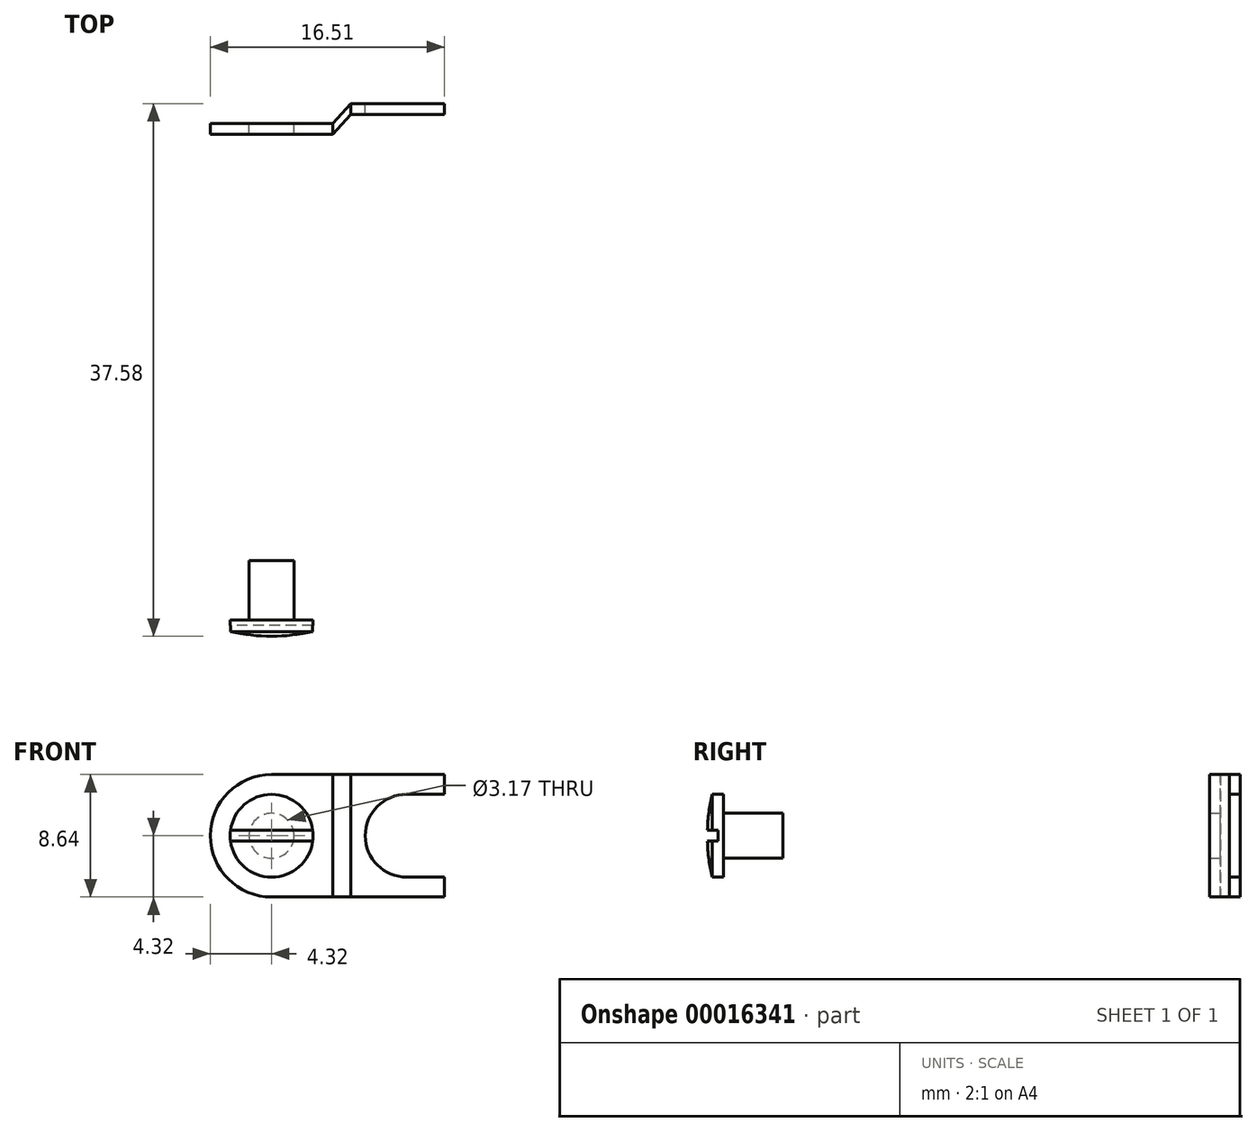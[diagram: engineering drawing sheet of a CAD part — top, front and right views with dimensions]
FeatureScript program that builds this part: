
annotation { "Feature Type Name" : "Feature", "Feature Type Description" : "" }
export const myFeature = defineFeature(function(context is Context, id is Id, definition is map)
    precondition{}
    {
        {
            var Q0;
            Q0=qCreatedBy(makeId("Front.planeOp"),FACE);
            var sketch = newSketch(context, id + "F0", { "sketchPlane" : qUnion([Q0])});
            skLineSegment(sketch, "E0.rect.bottom", {"start": v(4.32, -4.32) * mm, "end": v(0, -4.32) * mm});
            skLineSegment(sketch, "E0.rect.top", {"start": v(4.32, 4.32) * mm, "end": v(0, 4.32) * mm});
            skLineSegment(sketch, "E0.rect.left", {"start": v(4.32, -4.32) * mm, "end": v(4.32, 4.32) * mm});
            skLineSegment(sketch, "E0.rect.right", {"start": v(-4.32, 0) * mm, "end": v(-4.32, 0) * mm});
            skPoint(sketch, "E0.rect.middle", {"position": v(0, 0) * mm});
            skLineSegment(sketch, "E1.bottom", {"start": v(4.32, 4.32) * mm, "end": v(5.59, 4.32) * mm, "construction": true});
            skLineSegment(sketch, "E1.top", {"start": v(4.32, -4.32) * mm, "end": v(5.59, -4.32) * mm, "construction": true});
            skLineSegment(sketch, "E1.left", {"start": v(4.32, 4.32) * mm, "end": v(4.32, -4.32) * mm, "construction": true});
            skLineSegment(sketch, "E1.right", {"start": v(5.59, 4.32) * mm, "end": v(5.59, -4.32) * mm, "construction": true});
            skLineSegment(sketch, "E2.bottom", {"start": v(5.59, 4.32) * mm, "end": v(12.2, 4.32) * mm, "construction": true});
            skLineSegment(sketch, "E2.top", {"start": v(5.59, -4.32) * mm, "end": v(12.2, -4.32) * mm, "construction": true});
            skLineSegment(sketch, "E2.right", {"start": v(12.2, 4.32) * mm, "end": v(12.2, -4.32) * mm, "construction": true});
            skCircle(sketch, "E3", {"center": v(0, 0) * mm, "radius": 1.59 * mm});
            skPoint(sketch, "E4.visualSharp", {"position": v(-4.32, 4.32) * mm});
            skArc(sketch, "E4.filletArc", {"start": v(0, 4.32) * mm, "mid": v(-3.05, 3.05) * mm, "end": v(-4.32, 0) * mm});
            skPoint(sketch, "E5.visualSharp", {"position": v(-4.32, -4.32) * mm});
            skArc(sketch, "E5.filletArc", {"start": v(-4.32, 0) * mm, "mid": v(-3.05, -3.05) * mm, "end": v(0, -4.32) * mm});
            skSolve(sketch);
        }
        {
            var Q0;
            Q0=makeQuery(id+"F0.imprint","IMPRINT",FACE,{"disambiguationData":[TD([[makeQuery(id+"F0.imprint","IMPRINT",EDGE,{"derivedFrom":sQuery(id+"F0.wireOp",EDGE,"E0.rect.bottom")}),-1.0]])]});
            cPlane(context, id + "F1", {"entities" : qUnion([Q0]), "cplaneType" : CPlaneType.OFFSET, "offset" : 1.4 * mm, "oppositeDirection" : true, "width" : 152.4 * mm, "height" : 152.4 * mm});
        }
        {
            var Q0;
            Q0=qCreatedBy(id+"F1.planeOp",FACE);
            var sketch = newSketch(context, id + "F2", { "sketchPlane" : qUnion([Q0])});
            skPoint(sketch, "E6.0", {"position": v(5.59, 4.32) * mm});
            skPoint(sketch, "E7.0", {"position": v(5.59, -4.32) * mm});
            skPoint(sketch, "E8.0", {"position": v(12.2, -4.32) * mm});
            skPoint(sketch, "E9.0", {"position": v(12.2, 4.32) * mm});
            skLineSegment(sketch, "E10.bottom", {"start": v(5.59, 4.32) * mm, "end": v(12.2, 4.32) * mm});
            skLineSegment(sketch, "E10.top", {"start": v(5.59, -4.32) * mm, "end": v(12.2, -4.32) * mm});
            skLineSegment(sketch, "E10.left", {"start": v(5.59, 4.32) * mm, "end": v(5.59, -4.32) * mm});
            skLineSegment(sketch, "E10.right", {"start": v(12.2, 4.32) * mm, "end": v(12.2, -4.32) * mm});
            skLineSegment(sketch, "E11", {"start": v(12.2, 2.92) * mm, "end": v(5.59, 2.92) * mm});
            skPoint(sketch, "E12.0", {"position": v(0, 0) * mm});
            skLineSegment(sketch, "E13", {"start": v(5.59, 0) * mm, "end": v(12.2, 0) * mm, "construction": true});
            skLineSegment(sketch, "E14.MirrorCS", {"start": v(12.2, -2.92) * mm, "end": v(5.59, -2.92) * mm});
            skCircle(sketch, "E15", {"center": v(9.53, 0) * mm, "radius": 2.92 * mm});
            skSolve(sketch);
        }
        {
            var Q0;
            Q0 = qSketchRegion(id + "F0", true);
            extrude(context, id + "F3", {"entities" : qUnion([Q0]), "depth" : 0.76 * mm});
        }
        {
            var Q0;
            {var subQ6=sQuery(id+"F2.wireOp",EDGE,"E10.bottom");Q0=makeQuery(id+"F2.imprint","IMPRINT",FACE,{"disambiguationData":[TD([[makeQuery(id+"F2.imprint","IMPRINT",EDGE,{"derivedFrom":subQ6}),-1.0]])]});}
            var Q1;
            {var subQ6=sQuery(id+"F2.wireOp",EDGE,"E10.top");Q1=makeQuery(id+"F2.imprint","IMPRINT",FACE,{"disambiguationData":[TD([[makeQuery(id+"F2.imprint","IMPRINT",EDGE,{"derivedFrom":subQ6}),1.0]])]});}
            var Q2;
            {var subQ3=sQuery(id+"F2.wireOp",EDGE,"E11");var subQ5=sQuery(id+"F2.wireOp",EDGE,"E10.left");var subQ7=makeQuery(id+"F2.imprint","INTERSECT",VERTEX,{"derivedFrom":[subQ5,subQ3]});Q2=makeQuery(id+"F2.imprint","IMPRINT",FACE,{"disambiguationData":[TD([[makeQuery(id+"F2.imprint","IMPRINT",EDGE,{"disambiguationData":[TD([[subQ7,-1.0]])],"derivedFrom":subQ5}),1.0]])]});}
            extrude(context, id + "F4", {"entities" : qUnion([Q0, Q1, Q2]), "depth" : 0.76 * mm});
        }
        {
            var Q0;
            Q0=makeQuery(id+"F3.opExtrude","SWEPT_FACE",FACE,{"disambiguationData":[OSD([sQuery(id+"F0.wireOp",EDGE,"E0.rect.left")])]});
            var Q1;
            Q1=makeQuery(id+"F4.opExtrude","SWEPT_FACE",FACE,{"disambiguationData":[OSD([sQuery(id+"F2.wireOp",EDGE,"E10.left")])]});
            loft(context, id + "F5", {"sheetProfilesArray" : [{ "sheetProfileEntities" : qUnion([Q0]) }, { "sheetProfileEntities" : qUnion([Q1]) }]});
        }
        {
            var Q0;
            Q0=qCreatedBy(makeId("Right.planeOp"),FACE);
            var sketch = newSketch(context, id + "F6", { "sketchPlane" : qUnion([Q0])});
            skLineSegment(sketch, "E16.bottom", {"start": v(-35.04, 1.59) * mm, "end": v(-30.85, 1.59) * mm});
            skLineSegment(sketch, "E16.top", {"start": v(-35.04, 0) * mm, "end": v(-30.85, 0) * mm});
            skLineSegment(sketch, "E16.left", {"start": v(-35.04, 1.59) * mm, "end": v(-35.04, 0) * mm});
            skLineSegment(sketch, "E16.right", {"start": v(-30.85, 1.59) * mm, "end": v(-30.85, 0) * mm});
            skLineSegment(sketch, "E17.bottom", {"start": v(-36.18, 2.92) * mm, "end": v(-35.04, 2.92) * mm});
            skLineSegment(sketch, "E17.top", {"start": v(-36.18, 0) * mm, "end": v(-35.04, 0) * mm});
            skLineSegment(sketch, "E17.left", {"start": v(-36.18, 2.92) * mm, "end": v(-36.18, 0) * mm});
            skLineSegment(sketch, "E17.right", {"start": v(-35.04, 2.92) * mm, "end": v(-35.04, 0) * mm});
            skCircle(sketch, "E18", {"center": v(-23.48, 0) * mm, "radius": 12.7 * mm});
            skLineSegment(sketch, "E19", {"start": v(-36.18, 0) * mm, "end": v(-36.18, 2.92) * mm, "construction": true});
            skSolve(sketch);
        }
        {
            var Q0;
            Q0=qCreatedBy(makeId("Front.planeOp"),FACE);
            var Q1;
            Q1=sQuery(id+"F6.wireOp",VERTEX,"E17.top.start");
            cPlane(context, id + "F7", {"entities" : qUnion([Q0, Q1]), "cplaneType" : CPlaneType.PLANE_POINT, "offset" : 152.4 * mm, "width" : 152.4 * mm, "height" : 152.4 * mm});
        }
        {
            var Q0;
            {var subQ1=sQuery(id+"F6.wireOp",EDGE,"E17.top");Q0=makeQuery(id+"F6.imprint","IMPRINT",FACE,{"disambiguationData":[TD([[makeQuery(id+"F6.imprint","IMPRINT",EDGE,{"derivedFrom":subQ1}),1.0]])]});}
            var Q1;
            {var subQ2=sQuery(id+"F6.wireOp",EDGE,"E16.bottom");Q1=makeQuery(id+"F6.imprint","IMPRINT",FACE,{"disambiguationData":[TD([[makeQuery(id+"F6.imprint","IMPRINT",EDGE,{"derivedFrom":subQ2}),-1.0]])]});}
            var Q2;
            Q2=sQuery(id+"F6.wireOp",EDGE,"E16.top");
            revolve(context, id + "F8", {"entities" : qUnion([Q0, Q1]), "axis" : qUnion([Q2]), "revolveType" : RevolveType.FULL});
        }
        {
            var Q0;
            Q0=qCreatedBy(id+"F7.planeOp",FACE);
            var sketch = newSketch(context, id + "F9", { "sketchPlane" : qUnion([Q0])});
            skLineSegment(sketch, "E20.rect.bottom", {"start": v(4.53, 0.38) * mm, "end": v(-4.53, 0.38) * mm});
            skLineSegment(sketch, "E20.rect.top", {"start": v(4.53, -0.38) * mm, "end": v(-4.53, -0.38) * mm});
            skLineSegment(sketch, "E20.rect.left", {"start": v(4.53, 0.38) * mm, "end": v(4.53, -0.38) * mm});
            skLineSegment(sketch, "E20.rect.right", {"start": v(-4.53, 0.38) * mm, "end": v(-4.53, -0.38) * mm});
            skPoint(sketch, "E20.rect.middle", {"position": v(0, 0) * mm});
            skSolve(sketch);
        }
        {
            var Q0;
            Q0 = qSketchRegion(id + "F9", true);
            extrude(context, id + "F10", {"entities" : qUnion([Q0]), "operationType" : NewBodyOperationType.REMOVE, "oppositeDirection" : true, "depth" : 0.76 * mm});
        }
    });
